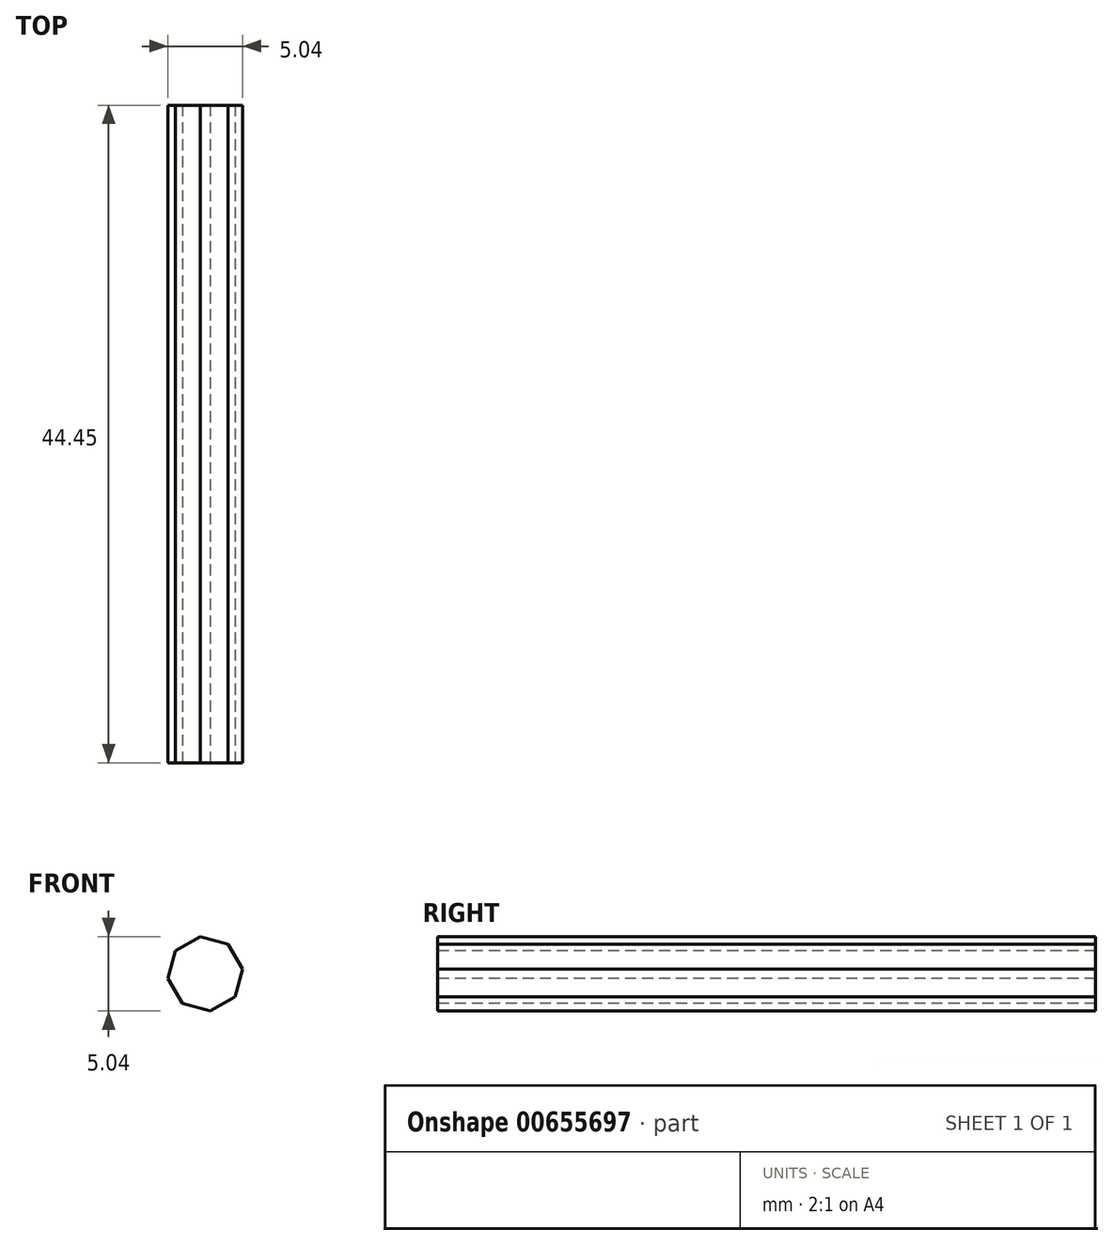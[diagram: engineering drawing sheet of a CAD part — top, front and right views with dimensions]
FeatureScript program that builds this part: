
annotation { "Feature Type Name" : "Feature", "Feature Type Description" : "" }
export const myFeature = defineFeature(function(context is Context, id is Id, definition is map)
    precondition{}
    {
        {
            var Q0;
            Q0=qCreatedBy(makeId("Front.planeOp"),FACE);
            var sketch = newSketch(context, id + "F0", { "sketchPlane" : qUnion([Q0])});
            skCircle(sketch, "E0.cCircle", {"center": v(0, 0) * mm, "radius": 2.54 * mm, "construction": true});
            skLineSegment(sketch, "E0.0", {"start": v(2.01, -1.55) * mm, "end": v(0.33, -2.52) * mm});
            skLineSegment(sketch, "E0.1", {"start": v(0.33, -2.52) * mm, "end": v(-1.55, -2.01) * mm});
            skLineSegment(sketch, "E0.2", {"start": v(-1.55, -2.01) * mm, "end": v(-2.52, -0.33) * mm});
            skLineSegment(sketch, "E0.3", {"start": v(-2.52, -0.33) * mm, "end": v(-2.01, 1.55) * mm});
            skLineSegment(sketch, "E0.4", {"start": v(-2.01, 1.55) * mm, "end": v(-0.33, 2.52) * mm});
            skLineSegment(sketch, "E0.5", {"start": v(-0.33, 2.52) * mm, "end": v(1.55, 2.01) * mm});
            skLineSegment(sketch, "E0.6", {"start": v(1.55, 2.01) * mm, "end": v(2.52, 0.33) * mm});
            skLineSegment(sketch, "E0.7", {"start": v(2.52, 0.33) * mm, "end": v(2.01, -1.55) * mm});
            skSolve(sketch);
        }
        {
            var Q0;
            Q0 = qSketchRegion(id + "F0", true);
            extrude(context, id + "F1", {"entities" : qUnion([Q0]), "oppositeDirection" : true, "depth" : 44.45 * mm, "offsetDistance" : 25.4 * mm});
        }
    });
